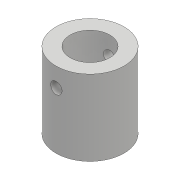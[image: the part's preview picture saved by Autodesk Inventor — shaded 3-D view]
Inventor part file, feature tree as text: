
AUTODESK INVENTOR PART (.ipt)
format: ipt  version: 2018 (Build 220112000, 112)  size: 96,256 bytes
history: native  units: mm
features: extrude x2, sketch x2
ambient origin geometry x8: Origin, YZ Plane, XZ Plane, XY Plane, X Axis, Y Axis, Z Axis, Center Point
bodies: Solid1 (feature_tree)
feature tree (4):
  extrude  "Extrusion1"  Depth=10.5mm
  extrude  "Extrusion2"  Depth=15.0mm
  sketch  "Sketch1"  dims[d0=18.0mm d1=10.5mm]
  sketch  "Sketch2"  dims[d2=20.0mm d3=0.0mm d4=15.0mm d5=3.0mm d6=20.0mm d7=0.0mm]
